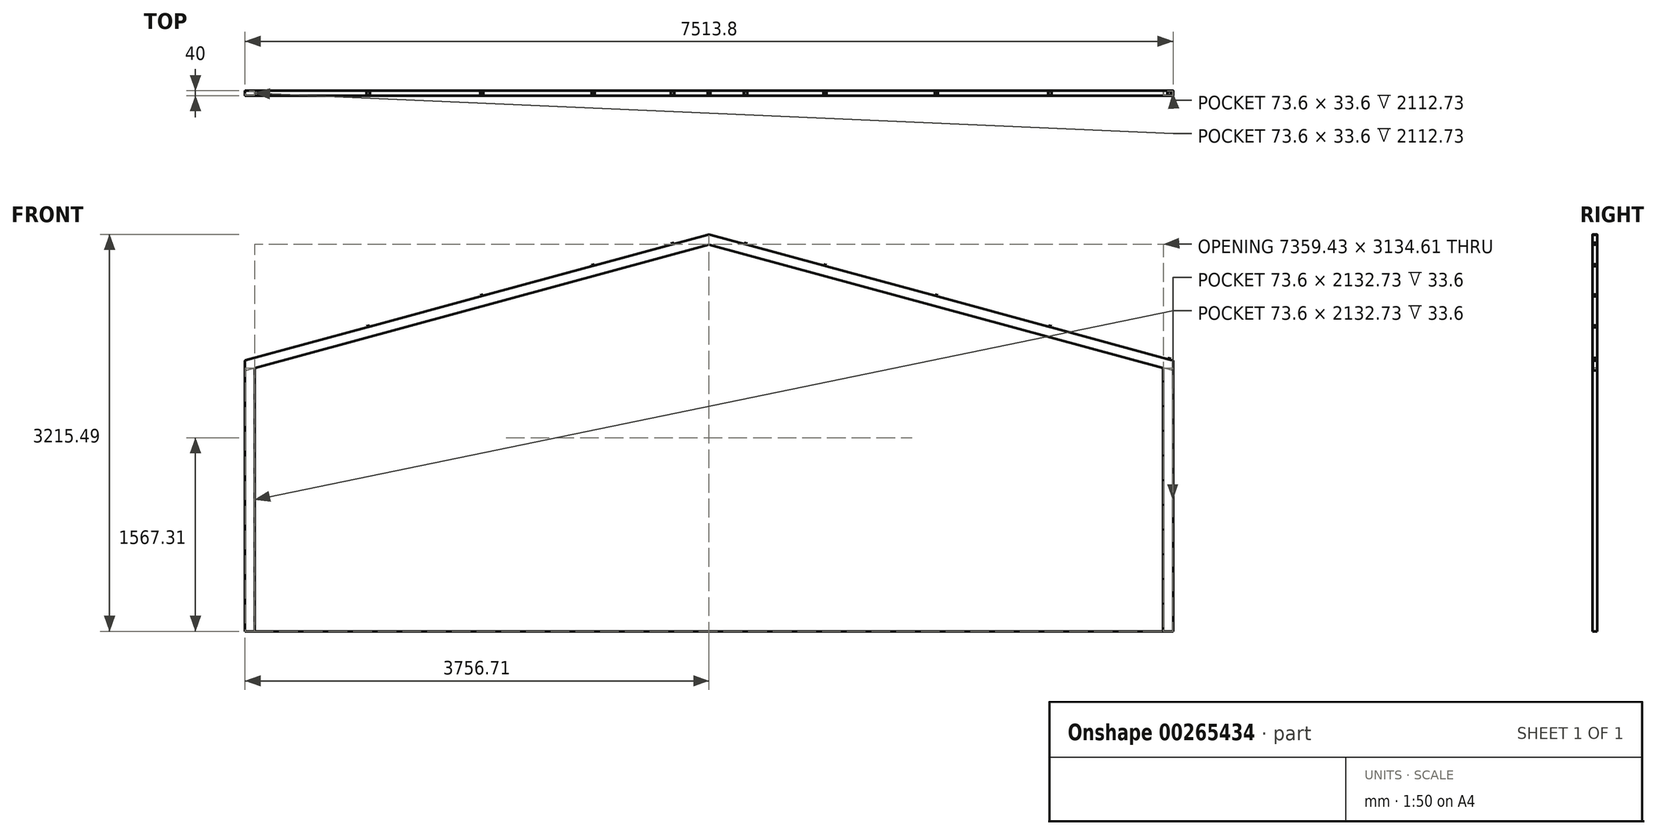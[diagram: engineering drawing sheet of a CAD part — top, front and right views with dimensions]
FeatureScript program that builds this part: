
annotation { "Feature Type Name" : "Feature", "Feature Type Description" : "" }
export const myFeature = defineFeature(function(context is Context, id is Id, definition is map)
    precondition{}
    {
        {
            var Q0;
            Q0=qCreatedBy(makeId("Top.planeOp"),FACE);
            var sketch = newSketch(context, id + "F0", { "sketchPlane" : qUnion([Q0])});
            skLineSegment(sketch, "E0.bottom", {"start": v(40, 20) * mm, "end": v(-40, 20) * mm});
            skLineSegment(sketch, "E0.top", {"start": v(40, -20) * mm, "end": v(-40, -20) * mm});
            skLineSegment(sketch, "E0.left", {"start": v(40, 20) * mm, "end": v(40, -20) * mm});
            skLineSegment(sketch, "E0.right", {"start": v(-40, 20) * mm, "end": v(-40, -20) * mm});
            skPoint(sketch, "E0.middle", {"position": v(0, 0) * mm});
            skLineSegment(sketch, "E1.bottom", {"start": v(-36.8, 16.8) * mm, "end": v(36.8, 16.8) * mm});
            skLineSegment(sketch, "E1.top", {"start": v(-36.8, -16.8) * mm, "end": v(36.8, -16.8) * mm});
            skLineSegment(sketch, "E1.left", {"start": v(-36.8, 16.8) * mm, "end": v(-36.8, -16.8) * mm});
            skLineSegment(sketch, "E1.right", {"start": v(36.8, 16.8) * mm, "end": v(36.8, -16.8) * mm});
            skSolve(sketch);
        }
        {
            var Q0;
            Q0=makeQuery(id+"F0.imprint","IMPRINT",FACE,{"disambiguationData":[TD([[makeQuery(id+"F0.imprint","IMPRINT",EDGE,{"derivedFrom":sQuery(id+"F0.wireOp",EDGE,"E0.bottom")}),1.0]])]});
            extrude(context, id + "F1", {"entities" : qUnion([Q0]), "depth" : 2133.6 * mm});
        }
        {
            var Q0;
            Q0=makeQuery(id+"F1.opExtrude","SWEPT_FACE",FACE,{"disambiguationData":[OSD([sQuery(id+"F0.wireOp",EDGE,"E0.top")])]});
            var sketch = newSketch(context, id + "F2", { "sketchPlane" : qUnion([Q0])});
            skLineSegment(sketch, "E2", {"start": v(40, 2133.6) * mm, "end": v(-40, 2111.86) * mm});
            skLineSegment(sketch, "E3", {"start": v(40, 2133.6) * mm, "end": v(19.02, 2210.8) * mm});
            skLineSegment(sketch, "E4", {"start": v(-40, 2111.86) * mm, "end": v(-60.98, 2189.07) * mm});
            skLineSegment(sketch, "E5", {"start": v(-60.98, 2189.07) * mm, "end": v(19.02, 2210.8) * mm});
            skLineSegment(sketch, "E6", {"start": v(-40, 2133.6) * mm, "end": v(-40, 2194.76) * mm});
            skSolve(sketch);
        }
        {
            var Q0;
            {var subQ0=sQuery(id+"F2.wireOp",EDGE,"E2");Q0=makeQuery(id+"F2.imprint","IMPRINT",FACE,{"disambiguationData":[TD([[makeQuery(id+"F2.imprint","IMPRINT",EDGE,{"derivedFrom":subQ0}),-1.0]])]});}
            extrude(context, id + "F3", {"entities" : qUnion([Q0]), "operationType" : NewBodyOperationType.REMOVE, "oppositeDirection" : true, "depth" : 40 * mm});
        }
        {
            var Q0;
            {var subQ0=sQuery(id+"F2.wireOp",EDGE,"E2");Q0=makeQuery(id+"F2.imprint","IMPRINT",FACE,{"disambiguationData":[TD([[makeQuery(id+"F2.imprint","IMPRINT",EDGE,{"derivedFrom":subQ0}),-1.0]])]});}
            var Q1;
            {var subQ0=sQuery(id+"F2.wireOp",EDGE,"E3");Q1=makeQuery(id+"F2.imprint","IMPRINT",FACE,{"disambiguationData":[TD([[makeQuery(id+"F2.imprint","IMPRINT",EDGE,{"derivedFrom":subQ0}),1.0]])]});}
            extrude(context, id + "F4", {"entities" : qUnion([Q0, Q1]), "operationType" : NewBodyOperationType.ADD, "oppositeDirection" : true, "depth" : 40 * mm});
        }
        {
            var Q0;
            Q0=makeQuery(id+"F4.opExtrude","SWEPT_FACE",FACE,{"disambiguationData":[OSD([sQuery(id+"F2.wireOp",EDGE,"E3")])]});
            var sketch = newSketch(context, id + "F5", { "sketchPlane" : qUnion([Q0])});
            skLineSegment(sketch, "E7.bottom", {"start": v(15.4, 2125.87) * mm, "end": v(-15.4, 2125.87) * mm});
            skLineSegment(sketch, "E7.top", {"start": v(15.4, 2051.07) * mm, "end": v(-15.4, 2051.07) * mm});
            skLineSegment(sketch, "E7.left", {"start": v(17.4, 2123.87) * mm, "end": v(17.4, 2053.07) * mm});
            skLineSegment(sketch, "E7.right", {"start": v(-17.4, 2123.87) * mm, "end": v(-17.4, 2053.07) * mm});
            skPoint(sketch, "E8.visualSharp", {"position": v(-17.4, 2125.87) * mm});
            skArc(sketch, "E8.filletArc", {"start": v(-15.4, 2125.87) * mm, "mid": v(-16.81, 2125.29) * mm, "end": v(-17.4, 2123.87) * mm});
            skPoint(sketch, "E9.visualSharp", {"position": v(17.4, 2125.87) * mm});
            skArc(sketch, "E9.filletArc", {"start": v(17.4, 2123.87) * mm, "mid": v(16.81, 2125.29) * mm, "end": v(15.4, 2125.87) * mm});
            skPoint(sketch, "E10.visualSharp", {"position": v(17.4, 2051.07) * mm});
            skArc(sketch, "E10.filletArc", {"start": v(15.4, 2051.07) * mm, "mid": v(16.81, 2051.66) * mm, "end": v(17.4, 2053.07) * mm});
            skPoint(sketch, "E11.visualSharp", {"position": v(-17.4, 2051.07) * mm});
            skArc(sketch, "E11.filletArc", {"start": v(-17.4, 2053.07) * mm, "mid": v(-16.81, 2051.66) * mm, "end": v(-15.4, 2051.07) * mm});
            skSolve(sketch);
        }
        {
            var Q0;
            Q0=makeQuery(id+"F5.imprint","IMPRINT",FACE,{"disambiguationData":[TD([[makeQuery(id+"F5.imprint","IMPRINT",EDGE,{"derivedFrom":sQuery(id+"F5.wireOp",EDGE,"E7.bottom")}),1.0]])]});
            extrude(context, id + "F6", {"entities" : qUnion([Q0]), "operationType" : NewBodyOperationType.REMOVE, "oppositeDirection" : true, "depth" : 92.3 * mm});
        }
        {
            var Q0;
            Q0=makeQuery(id+"F4.opExtrude","SWEPT_FACE",FACE,{"disambiguationData":[OSD([sQuery(id+"F2.wireOp",EDGE,"E3")])]});
            extrude(context, id + "F7", {"entities" : qUnion([Q0]), "operationType" : NewBodyOperationType.ADD, "depth" : 3810 * mm});
        }
        {
            var Q0;
            {var subQ0=sQuery(id+"F2.wireOp",EDGE,"E3");var subQ1=sQuery(id+"F0.wireOp",EDGE,"E0.top");Q0=makeQuery(id+"F7.boolean.opBoolean","MERGE",FACE,{"derivedFrom":[makeQuery(id+"F4.boolean.opBoolean","MERGE",FACE,{"derivedFrom":[makeQuery(id+"F1.opExtrude","SWEPT_FACE",FACE,{"disambiguationData":[OSD([subQ1])]}),makeQuery(id+"F4.opExtrude","CAP_FACE",FACE,{"disambiguationData":[OSD([subQ1,sQuery(id+"F0.wireOp",EDGE,"E0.right"),sQuery(id+"F2.wireOp",EDGE,"E2"),subQ0,sQuery(id+"F2.wireOp",EDGE,"E5"),sQuery(id+"F2.wireOp",EDGE,"E6")])],"isStart":true})]}),makeQuery(id+"F7.opExtrude","SWEPT_FACE",FACE,{"disambiguationData":[OSD([subQ0]),TDD([makeQuery(id+"F4.opExtrude","CAP_EDGE",EDGE,{"disambiguationData":[OSD([subQ0])],"isStart":true})])]})]});}
            var sketch = newSketch(context, id + "F8", { "sketchPlane" : qUnion([Q0])});
            skLineSegment(sketch, "E12", {"start": v(3695.74, 3209.74) * mm, "end": v(3716.71, 3215.44) * mm});
            skLineSegment(sketch, "E13", {"start": v(3716.71, 3132.54) * mm, "end": v(3716.71, 3215.44) * mm});
            skSolve(sketch);
        }
        {
            var Q0;
            Q0=makeQuery(id+"F8.imprint","IMPRINT",FACE,{"disambiguationData":[TD([[makeQuery(id+"F8.imprint","IMPRINT",EDGE,{"derivedFrom":sQuery(id+"F8.wireOp",EDGE,"E12")}),-1.0]])]});
            extrude(context, id + "F9", {"entities" : qUnion([Q0]), "operationType" : NewBodyOperationType.ADD, "oppositeDirection" : true, "depth" : 40 * mm});
        }
        {
            var Q0;
            Q0=makeQuery(id+"F9.opExtrude","SWEPT_FACE",FACE,{"disambiguationData":[OSD([sQuery(id+"F2.wireOp",EDGE,"E3")])]});
            extrude(context, id + "F10", {"entities" : qUnion([Q0]), "operationType" : NewBodyOperationType.REMOVE, "oppositeDirection" : true, "depth" : 558 * mm});
        }
        {
            var Q0;
            Q0=makeQuery(id+"F1.opExtrude","SWEPT_BODY",BODY,{"disambiguationData":[OSD([sQuery(id+"F0.wireOp",EDGE,"E0.bottom"),sQuery(id+"F0.wireOp",EDGE,"E0.top"),sQuery(id+"F0.wireOp",EDGE,"E0.left"),sQuery(id+"F0.wireOp",EDGE,"E0.right"),sQuery(id+"F0.wireOp",EDGE,"E1.bottom"),sQuery(id+"F0.wireOp",EDGE,"E1.top"),sQuery(id+"F0.wireOp",EDGE,"E1.left"),sQuery(id+"F0.wireOp",EDGE,"E1.right")])]});
            var Q1;
            Q1=makeQuery(id+"F9.opExtrude","SWEPT_FACE",FACE,{"disambiguationData":[OSD([sQuery(id+"F8.wireOp",EDGE,"E13")])]});
            mirror(context, id + "F11", {"operationType" : NewBodyOperationType.ADD, "entities" : qUnion([Q0]), "mirrorPlane" : qUnion([Q1])});
        }
        {
            var Q0;
            {var subQ0=sQuery(id+"F2.wireOp",EDGE,"E3");var subQ1=sQuery(id+"F0.wireOp",EDGE,"E0.top");var subQ2=makeQuery(id+"F9.boolean.opBoolean","MERGE",FACE,{"derivedFrom":[makeQuery(id+"F7.boolean.opBoolean","MERGE",FACE,{"derivedFrom":[makeQuery(id+"F4.boolean.opBoolean","MERGE",FACE,{"derivedFrom":[makeQuery(id+"F1.opExtrude","SWEPT_FACE",FACE,{"disambiguationData":[OSD([subQ1])]}),makeQuery(id+"F4.opExtrude","CAP_FACE",FACE,{"disambiguationData":[OSD([subQ1,sQuery(id+"F0.wireOp",EDGE,"E0.right"),sQuery(id+"F2.wireOp",EDGE,"E2"),subQ0,sQuery(id+"F2.wireOp",EDGE,"E5"),sQuery(id+"F2.wireOp",EDGE,"E6")])],"isStart":true})]}),makeQuery(id+"F7.opExtrude","SWEPT_FACE",FACE,{"disambiguationData":[OSD([subQ0]),TDD([makeQuery(id+"F4.opExtrude","CAP_EDGE",EDGE,{"disambiguationData":[OSD([subQ0])],"isStart":true})])]})]}),makeQuery(id+"F9.opExtrude","CAP_FACE",FACE,{"disambiguationData":[OSD([subQ0,sQuery(id+"F8.wireOp",EDGE,"E12"),sQuery(id+"F8.wireOp",EDGE,"E13")])],"isStart":true})]});Q0=makeQuery(id+"F11.boolean.opBoolean","MERGE",FACE,{"derivedFrom":[subQ2,makeQuery(id+"F11.opPattern","COPY",FACE,{"derivedFrom":subQ2,"instanceName":"1"})]});}
            var sketch = newSketch(context, id + "F12", { "sketchPlane" : qUnion([Q0])});
            skLineSegment(sketch, "E14", {"start": v(-6.28, 2203.93) * mm, "end": v(-18.35, 2200.65) * mm});
            skLineSegment(sketch, "E15", {"start": v(-6.28, 2203.93) * mm, "end": v(5.78, 2207.2) * mm});
            skLineSegment(sketch, "E16", {"start": v(-18.35, 2200.65) * mm, "end": v(5.78, 2207.2) * mm});
            skLineSegment(sketch, "E17", {"start": v(-18.35, 2200.65) * mm, "end": v(-20.97, 2210.3) * mm});
            skLineSegment(sketch, "E18", {"start": v(5.78, 2207.2) * mm, "end": v(3.16, 2216.85) * mm});
            skLineSegment(sketch, "E19", {"start": v(-20.97, 2210.3) * mm, "end": v(3.16, 2216.85) * mm});
            skLineSegment(sketch, "E20", {"start": v(40, 2133.6) * mm, "end": v(40, 2216.5) * mm});
            skLineSegment(sketch, "E21", {"start": v(40, 2216.5) * mm, "end": v(959.18, 2466.24) * mm});
            skLineSegment(sketch, "E22", {"start": v(959.18, 2466.24) * mm, "end": v(971.24, 2469.51) * mm});
            skLineSegment(sketch, "E23", {"start": v(959.18, 2466.24) * mm, "end": v(947.12, 2462.96) * mm});
            skLineSegment(sketch, "E24", {"start": v(947.12, 2462.96) * mm, "end": v(944.5, 2472.6) * mm});
            skLineSegment(sketch, "E25", {"start": v(971.24, 2469.51) * mm, "end": v(968.62, 2479.16) * mm});
            skLineSegment(sketch, "E26", {"start": v(944.5, 2472.6) * mm, "end": v(968.62, 2479.16) * mm});
            skLineSegment(sketch, "E27", {"start": v(40, 2216.5) * mm, "end": v(1878.36, 2715.97) * mm});
            skLineSegment(sketch, "E28", {"start": v(1878.36, 2715.97) * mm, "end": v(1890.42, 2719.25) * mm});
            skLineSegment(sketch, "E29", {"start": v(1878.36, 2715.97) * mm, "end": v(1866.3, 2712.7) * mm});
            skLineSegment(sketch, "E30", {"start": v(1866.3, 2712.7) * mm, "end": v(1863.67, 2722.34) * mm});
            skLineSegment(sketch, "E31", {"start": v(1890.42, 2719.25) * mm, "end": v(1887.8, 2728.9) * mm});
            skLineSegment(sketch, "E32", {"start": v(1863.67, 2722.34) * mm, "end": v(1887.8, 2728.9) * mm});
            skLineSegment(sketch, "E33", {"start": v(2779.68, 2960.86) * mm, "end": v(2791.74, 2964.13) * mm});
            skLineSegment(sketch, "E34", {"start": v(2779.68, 2960.86) * mm, "end": v(2767.62, 2957.58) * mm});
            skLineSegment(sketch, "E35", {"start": v(2767.62, 2957.58) * mm, "end": v(2765, 2967.23) * mm});
            skLineSegment(sketch, "E36", {"start": v(2791.74, 2964.13) * mm, "end": v(2789.12, 2973.78) * mm});
            skLineSegment(sketch, "E37", {"start": v(2767.62, 2957.58) * mm, "end": v(2779.68, 2960.86) * mm});
            skLineSegment(sketch, "E38", {"start": v(2779.68, 2960.86) * mm, "end": v(40, 2216.5) * mm});
            skLineSegment(sketch, "E39", {"start": v(2765, 2967.23) * mm, "end": v(2789.12, 2973.78) * mm});
            skLineSegment(sketch, "E40", {"start": v(3422.38, 3135.47) * mm, "end": v(3410.32, 3132.2) * mm});
            skLineSegment(sketch, "E41", {"start": v(3422.38, 3135.47) * mm, "end": v(3434.45, 3138.75) * mm});
            skLineSegment(sketch, "E42", {"start": v(3434.45, 3138.75) * mm, "end": v(3431.82, 3148.4) * mm});
            skLineSegment(sketch, "E43", {"start": v(3431.82, 3148.4) * mm, "end": v(3407.7, 3141.85) * mm});
            skLineSegment(sketch, "E44", {"start": v(3407.7, 3141.85) * mm, "end": v(3410.32, 3132.2) * mm});
            skLineSegment(sketch, "E45", {"start": v(3716.71, 3215.44) * mm, "end": v(3716.71, 3204.23) * mm});
            skLineSegment(sketch, "E46.MirrorCS", {"start": v(4011.04, 3135.47) * mm, "end": v(4023.1, 3132.2) * mm});
            skLineSegment(sketch, "E47.MirrorCS", {"start": v(4011.04, 3135.47) * mm, "end": v(3998.98, 3138.75) * mm});
            skLineSegment(sketch, "E48.MirrorCS", {"start": v(3998.98, 3138.75) * mm, "end": v(4001.6, 3148.4) * mm});
            skLineSegment(sketch, "E49.MirrorCS", {"start": v(4001.6, 3148.4) * mm, "end": v(4025.73, 3141.85) * mm});
            skLineSegment(sketch, "E50.MirrorCS", {"start": v(4025.73, 3141.85) * mm, "end": v(4023.1, 3132.2) * mm});
            skLineSegment(sketch, "E51.MirrorCS", {"start": v(4665.8, 2957.58) * mm, "end": v(4668.43, 2967.23) * mm});
            skLineSegment(sketch, "E52.MirrorCS", {"start": v(4668.43, 2967.23) * mm, "end": v(4644.3, 2973.78) * mm});
            skLineSegment(sketch, "E53.MirrorCS", {"start": v(4641.68, 2964.13) * mm, "end": v(4644.3, 2973.78) * mm});
            skLineSegment(sketch, "E54.MirrorCS", {"start": v(4653.74, 2960.86) * mm, "end": v(4641.68, 2964.13) * mm});
            skLineSegment(sketch, "E55.MirrorCS", {"start": v(5555.07, 2715.97) * mm, "end": v(5567.13, 2712.7) * mm});
            skLineSegment(sketch, "E56.MirrorCS", {"start": v(5569.75, 2722.34) * mm, "end": v(5545.63, 2728.9) * mm});
            skLineSegment(sketch, "E57.MirrorCS", {"start": v(5543, 2719.25) * mm, "end": v(5545.63, 2728.9) * mm});
            skLineSegment(sketch, "E58.MirrorCS", {"start": v(5567.13, 2712.7) * mm, "end": v(5569.75, 2722.34) * mm});
            skLineSegment(sketch, "E59.MirrorCS", {"start": v(6486.31, 2462.96) * mm, "end": v(6488.93, 2472.6) * mm});
            skLineSegment(sketch, "E60.MirrorCS", {"start": v(6488.93, 2472.6) * mm, "end": v(6464.8, 2479.16) * mm});
            skLineSegment(sketch, "E61.MirrorCS", {"start": v(6462.18, 2469.51) * mm, "end": v(6464.8, 2479.16) * mm});
            skLineSegment(sketch, "E62.MirrorCS", {"start": v(6474.25, 2466.24) * mm, "end": v(6462.18, 2469.51) * mm});
            skLineSegment(sketch, "E63.MirrorCS", {"start": v(7451.77, 2200.65) * mm, "end": v(7427.65, 2207.2) * mm});
            skLineSegment(sketch, "E64.MirrorCS", {"start": v(7451.77, 2200.65) * mm, "end": v(7454.4, 2210.3) * mm});
            skLineSegment(sketch, "E65.MirrorCS", {"start": v(7454.4, 2210.3) * mm, "end": v(7430.27, 2216.85) * mm});
            skLineSegment(sketch, "E66.MirrorCS", {"start": v(7427.65, 2207.2) * mm, "end": v(7430.27, 2216.85) * mm});
            skLineSegment(sketch, "E67", {"start": v(4653.74, 2960.86) * mm, "end": v(4665.8, 2957.58) * mm});
            skLineSegment(sketch, "E68", {"start": v(5555.07, 2715.97) * mm, "end": v(5543, 2719.25) * mm});
            skLineSegment(sketch, "E69", {"start": v(6474.25, 2466.24) * mm, "end": v(6486.31, 2462.96) * mm});
            skLineSegment(sketch, "E70", {"start": v(3716.71, 3215.44) * mm, "end": v(3422.38, 3135.47) * mm});
            skLineSegment(sketch, "E71", {"start": v(3716.71, 3215.44) * mm, "end": v(3716.71, 3215.5) * mm});
            skLineSegment(sketch, "E72", {"start": v(3716.71, 3215.44) * mm, "end": v(3704.65, 3212.16) * mm});
            skLineSegment(sketch, "E73", {"start": v(3716.71, 3215.44) * mm, "end": v(3728.78, 3212.16) * mm});
            skLineSegment(sketch, "E74", {"start": v(3704.65, 3212.16) * mm, "end": v(3704.65, 3212.21) * mm});
            skLineSegment(sketch, "E75", {"start": v(3728.78, 3212.16) * mm, "end": v(3728.78, 3212.21) * mm});
            skLineSegment(sketch, "E76", {"start": v(3728.78, 3212.21) * mm, "end": v(3716.71, 3215.5) * mm});
            skLineSegment(sketch, "E77", {"start": v(3716.71, 3215.5) * mm, "end": v(3704.65, 3212.21) * mm});
            skSolve(sketch);
        }
        {
            var Q0;
            {var subQ0=sQuery(id+"F2.wireOp",EDGE,"E5");var subQ1=sQuery(id+"F2.wireOp",EDGE,"E3");Q0=makeQuery(id+"F9.boolean.opBoolean","MERGE",EDGE,{"derivedFrom":[makeQuery(id+"F7.boolean.opBoolean","MERGE",EDGE,{"derivedFrom":[makeQuery(id+"F4.opExtrude","CAP_EDGE",EDGE,{"disambiguationData":[OSD([subQ0])],"isStart":false}),makeQuery(id+"F7.opExtrude","SWEPT_EDGE",EDGE,{"disambiguationData":[OSD([subQ1,subQ0]),TDD([makeQuery(id+"F4.opExtrude","CAP_VERTEX",VERTEX,{"disambiguationData":[OSD([subQ1,subQ0])],"isStart":false})])]})]}),makeQuery(id+"F9.opExtrude","CAP_EDGE",EDGE,{"disambiguationData":[OSD([sQuery(id+"F8.wireOp",EDGE,"E12")])],"isStart":false})]});}
            var Q1;
            {var subQ0=sQuery(id+"F2.wireOp",EDGE,"E5");var subQ1=sQuery(id+"F2.wireOp",EDGE,"E3");Q1=makeQuery(id+"F11.opPattern","COPY",EDGE,{"derivedFrom":makeQuery(id+"F9.boolean.opBoolean","MERGE",EDGE,{"derivedFrom":[makeQuery(id+"F7.boolean.opBoolean","MERGE",EDGE,{"derivedFrom":[makeQuery(id+"F4.opExtrude","CAP_EDGE",EDGE,{"disambiguationData":[OSD([subQ0])],"isStart":false}),makeQuery(id+"F7.opExtrude","SWEPT_EDGE",EDGE,{"disambiguationData":[OSD([subQ1,subQ0]),TDD([makeQuery(id+"F4.opExtrude","CAP_VERTEX",VERTEX,{"disambiguationData":[OSD([subQ1,subQ0])],"isStart":false})])]})]}),makeQuery(id+"F9.opExtrude","CAP_EDGE",EDGE,{"disambiguationData":[OSD([sQuery(id+"F8.wireOp",EDGE,"E12")])],"isStart":false})]}),"instanceName":"1"});}
            var Q2;
            {var subQ0=sQuery(id+"F2.wireOp",EDGE,"E5");var subQ1=sQuery(id+"F2.wireOp",EDGE,"E3");Q2=makeQuery(id+"F11.opPattern","COPY",EDGE,{"derivedFrom":makeQuery(id+"F9.boolean.opBoolean","MERGE",EDGE,{"derivedFrom":[makeQuery(id+"F7.boolean.opBoolean","MERGE",EDGE,{"derivedFrom":[makeQuery(id+"F4.opExtrude","CAP_EDGE",EDGE,{"disambiguationData":[OSD([subQ0])],"isStart":true}),makeQuery(id+"F7.opExtrude","SWEPT_EDGE",EDGE,{"disambiguationData":[OSD([subQ1,subQ0]),TDD([makeQuery(id+"F4.opExtrude","CAP_VERTEX",VERTEX,{"disambiguationData":[OSD([subQ1,subQ0])],"isStart":true})])]})]}),makeQuery(id+"F9.opExtrude","CAP_EDGE",EDGE,{"disambiguationData":[OSD([sQuery(id+"F8.wireOp",EDGE,"E12")])],"isStart":true})]}),"instanceName":"1"});}
            var Q3;
            {var subQ0=sQuery(id+"F2.wireOp",EDGE,"E5");var subQ1=sQuery(id+"F2.wireOp",EDGE,"E3");Q3=makeQuery(id+"F9.boolean.opBoolean","MERGE",EDGE,{"derivedFrom":[makeQuery(id+"F7.boolean.opBoolean","MERGE",EDGE,{"derivedFrom":[makeQuery(id+"F4.opExtrude","CAP_EDGE",EDGE,{"disambiguationData":[OSD([subQ0])],"isStart":true}),makeQuery(id+"F7.opExtrude","SWEPT_EDGE",EDGE,{"disambiguationData":[OSD([subQ1,subQ0]),TDD([makeQuery(id+"F4.opExtrude","CAP_VERTEX",VERTEX,{"disambiguationData":[OSD([subQ1,subQ0])],"isStart":true})])]})]}),makeQuery(id+"F9.opExtrude","CAP_EDGE",EDGE,{"disambiguationData":[OSD([sQuery(id+"F8.wireOp",EDGE,"E12")])],"isStart":true})]});}
            var Q4;
            Q4=makeQuery(id+"F11.opPattern","COPY",EDGE,{"derivedFrom":makeQuery(id+"F7.opExtrude","SWEPT_EDGE",EDGE,{"disambiguationData":[OSD([sQuery(id+"F0.wireOp",EDGE,"E0.bottom"),sQuery(id+"F0.wireOp",EDGE,"E0.top"),sQuery(id+"F0.wireOp",EDGE,"E0.left"),sQuery(id+"F2.wireOp",EDGE,"E2"),sQuery(id+"F2.wireOp",EDGE,"E3")])]}),"instanceName":"1"});
            var Q5;
            Q5=makeQuery(id+"F7.opExtrude","SWEPT_EDGE",EDGE,{"disambiguationData":[OSD([sQuery(id+"F0.wireOp",EDGE,"E0.bottom"),sQuery(id+"F0.wireOp",EDGE,"E0.top"),sQuery(id+"F0.wireOp",EDGE,"E0.left"),sQuery(id+"F2.wireOp",EDGE,"E2"),sQuery(id+"F2.wireOp",EDGE,"E3")])]});
            var Q6;
            Q6=makeQuery(id+"F7.opExtrude","SWEPT_EDGE",EDGE,{"disambiguationData":[OSD([sQuery(id+"F0.wireOp",EDGE,"E0.top"),sQuery(id+"F0.wireOp",EDGE,"E0.left"),sQuery(id+"F2.wireOp",EDGE,"E2"),sQuery(id+"F2.wireOp",EDGE,"E3")])]});
            var Q7;
            Q7=makeQuery(id+"F11.opPattern","COPY",EDGE,{"derivedFrom":makeQuery(id+"F7.opExtrude","SWEPT_EDGE",EDGE,{"disambiguationData":[OSD([sQuery(id+"F0.wireOp",EDGE,"E0.top"),sQuery(id+"F0.wireOp",EDGE,"E0.left"),sQuery(id+"F2.wireOp",EDGE,"E2"),sQuery(id+"F2.wireOp",EDGE,"E3")])]}),"instanceName":"1"});
            fillet(context, id + "F13", {"entities" : qUnion([Q0, Q1, Q2, Q3, Q4, Q5, Q6, Q7]), "radius" : 2 * mm, "tangentPropagation" : true, "allowEdgeOverflow" : false});
        }
        {
            var Q0;
            Q0=makeQuery(id+"F1.opExtrude","SWEPT_EDGE",EDGE,{"disambiguationData":[OSD([sQuery(id+"F0.wireOp",EDGE,"E0.top"),sQuery(id+"F0.wireOp",EDGE,"E0.left")])]});
            var Q1;
            Q1=makeQuery(id+"F1.opExtrude","SWEPT_EDGE",EDGE,{"disambiguationData":[OSD([sQuery(id+"F0.wireOp",EDGE,"E0.bottom"),sQuery(id+"F0.wireOp",EDGE,"E0.left")])]});
            var Q2;
            {var subQ0=sQuery(id+"F0.wireOp",EDGE,"E0.right");Q2=makeQuery(id+"F4.boolean.opBoolean","MERGE",EDGE,{"derivedFrom":[makeQuery(id+"F1.opExtrude","SWEPT_EDGE",EDGE,{"disambiguationData":[OSD([sQuery(id+"F0.wireOp",EDGE,"E0.bottom"),subQ0])]}),makeQuery(id+"F4.opExtrude","CAP_EDGE",EDGE,{"disambiguationData":[OSD([sQuery(id+"F0.wireOp",EDGE,"E0.top"),subQ0,sQuery(id+"F2.wireOp",EDGE,"E6")])],"isStart":false})]});}
            var Q3;
            {var subQ0=sQuery(id+"F0.wireOp",EDGE,"E0.right");var subQ1=sQuery(id+"F0.wireOp",EDGE,"E0.top");Q3=makeQuery(id+"F11.opPattern","COPY",EDGE,{"derivedFrom":makeQuery(id+"F4.boolean.opBoolean","MERGE",EDGE,{"derivedFrom":[makeQuery(id+"F1.opExtrude","SWEPT_EDGE",EDGE,{"disambiguationData":[OSD([subQ1,subQ0])]}),makeQuery(id+"F4.opExtrude","CAP_EDGE",EDGE,{"disambiguationData":[OSD([subQ1,subQ0,sQuery(id+"F2.wireOp",EDGE,"E6")])],"isStart":true})]}),"instanceName":"1"});}
            var Q4;
            {var subQ0=sQuery(id+"F0.wireOp",EDGE,"E0.right");Q4=makeQuery(id+"F11.opPattern","COPY",EDGE,{"derivedFrom":makeQuery(id+"F4.boolean.opBoolean","MERGE",EDGE,{"derivedFrom":[makeQuery(id+"F1.opExtrude","SWEPT_EDGE",EDGE,{"disambiguationData":[OSD([sQuery(id+"F0.wireOp",EDGE,"E0.bottom"),subQ0])]}),makeQuery(id+"F4.opExtrude","CAP_EDGE",EDGE,{"disambiguationData":[OSD([sQuery(id+"F0.wireOp",EDGE,"E0.top"),subQ0,sQuery(id+"F2.wireOp",EDGE,"E6")])],"isStart":false})]}),"instanceName":"1"});}
            var Q5;
            Q5=makeQuery(id+"F11.opPattern","COPY",EDGE,{"derivedFrom":makeQuery(id+"F1.opExtrude","SWEPT_EDGE",EDGE,{"disambiguationData":[OSD([sQuery(id+"F0.wireOp",EDGE,"E0.bottom"),sQuery(id+"F0.wireOp",EDGE,"E0.left")])]}),"instanceName":"1"});
            var Q6;
            Q6=makeQuery(id+"F11.opPattern","COPY",EDGE,{"derivedFrom":makeQuery(id+"F1.opExtrude","SWEPT_EDGE",EDGE,{"disambiguationData":[OSD([sQuery(id+"F0.wireOp",EDGE,"E0.top"),sQuery(id+"F0.wireOp",EDGE,"E0.left")])]}),"instanceName":"1"});
            fillet(context, id + "F14", {"entities" : qUnion([Q0, Q1, Q2, Q3, Q4, Q5, Q6]), "radius" : 3 * mm, "tangentPropagation" : true, "allowEdgeOverflow" : false});
        }
        {
            var Q0;
            {var subQ0=sQuery(id+"F0.wireOp",EDGE,"E0.right");Q0=makeQuery(id+"F14.opFillet","SPLIT",FACE,{"disambiguationData":[OD(1.0)],"derivedFrom":makeQuery(id+"F4.boolean.opBoolean","MERGE",FACE,{"derivedFrom":[makeQuery(id+"F1.opExtrude","SWEPT_FACE",FACE,{"disambiguationData":[OSD([subQ0])]}),makeQuery(id+"F4.opExtrude","SWEPT_FACE",FACE,{"disambiguationData":[OSD([sQuery(id+"F0.wireOp",EDGE,"E0.top"),subQ0,sQuery(id+"F2.wireOp",EDGE,"E6")])]})]})});}
            var sketch = newSketch(context, id + "F15", { "sketchPlane" : qUnion([Q0])});
            skLineSegment(sketch, "E78", {"start": v(0, 0) * mm, "end": v(-20, 0) * mm});
            skLineSegment(sketch, "E79.bottom", {"start": v(-20, 0) * mm, "end": v(20, 0) * mm});
            skLineSegment(sketch, "E79.top", {"start": v(-20, 0) * mm, "end": v(20, 0) * mm});
            skLineSegment(sketch, "E79.left", {"start": v(-20, 0) * mm, "end": v(-20, 0) * mm});
            skLineSegment(sketch, "E79.right", {"start": v(20, 0) * mm, "end": v(20, 0) * mm});
            skSolve(sketch);
        }
        {
            var Q0;
            Q0=makeQuery(id+"F15.imprint","IMPRINT",FACE,{"disambiguationData":[TD([[makeQuery(id+"F15.imprint","IMPRINT",EDGE,{"derivedFrom":sQuery(id+"F15.wireOp",EDGE,"E79.top")}),1.0]])]});
            extrude(context, id + "F16", {"entities" : qUnion([Q0]), "operationType" : NewBodyOperationType.ADD, "oppositeDirection" : true, "depth" : 7513.8 * mm});
        }
        {
            var Q0;
            Q0=makeQuery(id+"F12.imprint","IMPRINT",FACE,{"disambiguationData":[TD([[makeQuery(id+"F12.imprint","IMPRINT",EDGE,{"derivedFrom":sQuery(id+"F12.wireOp",EDGE,"E16")}),1.0]])]});
            var Q1;
            {var subQ1=sQuery(id+"F12.wireOp",EDGE,"E24");Q1=makeQuery(id+"F12.imprint","IMPRINT",FACE,{"disambiguationData":[TD([[makeQuery(id+"F12.imprint","IMPRINT",EDGE,{"derivedFrom":subQ1}),-1.0]])]});}
            var Q2;
            {var subQ1=sQuery(id+"F12.wireOp",EDGE,"E30");Q2=makeQuery(id+"F12.imprint","IMPRINT",FACE,{"disambiguationData":[TD([[makeQuery(id+"F12.imprint","IMPRINT",EDGE,{"derivedFrom":subQ1}),-1.0]])]});}
            var Q3;
            {var subQ1=sQuery(id+"F12.wireOp",EDGE,"E35");Q3=makeQuery(id+"F12.imprint","IMPRINT",FACE,{"disambiguationData":[TD([[makeQuery(id+"F12.imprint","IMPRINT",EDGE,{"derivedFrom":subQ1}),-1.0]])]});}
            var Q4;
            Q4=makeQuery(id+"F12.imprint","IMPRINT",FACE,{"disambiguationData":[TD([[makeQuery(id+"F12.imprint","IMPRINT",EDGE,{"derivedFrom":sQuery(id+"F12.wireOp",EDGE,"E40")}),1.0]])]});
            var Q5;
            {var subQ7=sQuery(id+"F12.wireOp",EDGE,"rvYJcqt1-21Oj-p3wZ-czKF-GlUjLanXVYOE");Q5=makeQuery(id+"F12.imprint","IMPRINT",FACE,{"disambiguationData":[TD([[makeQuery(id+"F12.imprint","IMPRINT",EDGE,{"derivedFrom":subQ7}),-1.0]])]});}
            var Q6;
            Q6=makeQuery(id+"F12.imprint","IMPRINT",FACE,{"disambiguationData":[TD([[makeQuery(id+"F12.imprint","IMPRINT",EDGE,{"derivedFrom":sQuery(id+"F12.wireOp",EDGE,"E46.MirrorCS")}),-1.0]])]});
            var Q7;
            Q7=makeQuery(id+"F12.imprint","IMPRINT",FACE,{"disambiguationData":[TD([[makeQuery(id+"F12.imprint","IMPRINT",EDGE,{"derivedFrom":sQuery(id+"F12.wireOp",EDGE,"E51.MirrorCS")}),1.0]])]});
            var Q8;
            Q8=makeQuery(id+"F12.imprint","IMPRINT",FACE,{"disambiguationData":[TD([[makeQuery(id+"F12.imprint","IMPRINT",EDGE,{"derivedFrom":sQuery(id+"F12.wireOp",EDGE,"E55.MirrorCS")}),-1.0]])]});
            var Q9;
            Q9=makeQuery(id+"F12.imprint","IMPRINT",FACE,{"disambiguationData":[TD([[makeQuery(id+"F12.imprint","IMPRINT",EDGE,{"derivedFrom":sQuery(id+"F12.wireOp",EDGE,"E59.MirrorCS")}),1.0]])]});
            var Q10;
            Q10=makeQuery(id+"F12.imprint","IMPRINT",FACE,{"disambiguationData":[TD([[makeQuery(id+"F12.imprint","IMPRINT",EDGE,{"derivedFrom":sQuery(id+"F12.wireOp",EDGE,"E63.MirrorCS")}),-1.0]])]});
            extrude(context, id + "F17", {"entities" : qUnion([Q0, Q1, Q2, Q3, Q4, Q5, Q6, Q7, Q8, Q9, Q10]), "operationType" : NewBodyOperationType.ADD, "oppositeDirection" : true, "depth" : 40 * mm});
        }
        {
            var Q0;
            Q0=makeQuery(id+"F12.imprint","IMPRINT",FACE,{"disambiguationData":[TD([[makeQuery(id+"F12.imprint","IMPRINT",EDGE,{"derivedFrom":sQuery(id+"F12.wireOp",EDGE,"E16")}),1.0]])]});
            var Q1;
            {var subQ1=sQuery(id+"F12.wireOp",EDGE,"E24");Q1=makeQuery(id+"F12.imprint","IMPRINT",FACE,{"disambiguationData":[TD([[makeQuery(id+"F12.imprint","IMPRINT",EDGE,{"derivedFrom":subQ1}),-1.0]])]});}
            var Q2;
            {var subQ1=sQuery(id+"F12.wireOp",EDGE,"E30");Q2=makeQuery(id+"F12.imprint","IMPRINT",FACE,{"disambiguationData":[TD([[makeQuery(id+"F12.imprint","IMPRINT",EDGE,{"derivedFrom":subQ1}),-1.0]])]});}
            var Q3;
            {var subQ1=sQuery(id+"F12.wireOp",EDGE,"E33");Q3=makeQuery(id+"F12.imprint","IMPRINT",FACE,{"disambiguationData":[TD([[makeQuery(id+"F12.imprint","IMPRINT",EDGE,{"derivedFrom":subQ1}),1.0]])]});}
            var Q4;
            {var subQ1=sQuery(id+"F12.wireOp",EDGE,"E40");Q4=makeQuery(id+"F12.imprint","IMPRINT",FACE,{"disambiguationData":[TD([[makeQuery(id+"F12.imprint","IMPRINT",EDGE,{"derivedFrom":subQ1}),1.0]])]});}
            var Q5;
            Q5=makeQuery(id+"F12.imprint","IMPRINT",FACE,{"disambiguationData":[TD([[makeQuery(id+"F12.imprint","IMPRINT",EDGE,{"derivedFrom":sQuery(id+"F12.wireOp",EDGE,"E71")}),1.0]])]});
            var Q6;
            Q6=makeQuery(id+"F12.imprint","IMPRINT",FACE,{"disambiguationData":[TD([[makeQuery(id+"F12.imprint","IMPRINT",EDGE,{"derivedFrom":sQuery(id+"F12.wireOp",EDGE,"E71")}),-1.0]])]});
            var Q7;
            Q7=makeQuery(id+"F12.imprint","IMPRINT",FACE,{"disambiguationData":[TD([[makeQuery(id+"F12.imprint","IMPRINT",EDGE,{"derivedFrom":sQuery(id+"F12.wireOp",EDGE,"E46.MirrorCS")}),-1.0]])]});
            var Q8;
            Q8=makeQuery(id+"F12.imprint","IMPRINT",FACE,{"disambiguationData":[TD([[makeQuery(id+"F12.imprint","IMPRINT",EDGE,{"derivedFrom":sQuery(id+"F12.wireOp",EDGE,"E51.MirrorCS")}),1.0]])]});
            var Q9;
            Q9=makeQuery(id+"F12.imprint","IMPRINT",FACE,{"disambiguationData":[TD([[makeQuery(id+"F12.imprint","IMPRINT",EDGE,{"derivedFrom":sQuery(id+"F12.wireOp",EDGE,"E55.MirrorCS")}),-1.0]])]});
            var Q10;
            Q10=makeQuery(id+"F12.imprint","IMPRINT",FACE,{"disambiguationData":[TD([[makeQuery(id+"F12.imprint","IMPRINT",EDGE,{"derivedFrom":sQuery(id+"F12.wireOp",EDGE,"E59.MirrorCS")}),1.0]])]});
            var Q11;
            Q11=makeQuery(id+"F12.imprint","IMPRINT",FACE,{"disambiguationData":[TD([[makeQuery(id+"F12.imprint","IMPRINT",EDGE,{"derivedFrom":sQuery(id+"F12.wireOp",EDGE,"E63.MirrorCS")}),-1.0]])]});
            extrude(context, id + "F18", {"entities" : qUnion([Q0, Q1, Q2, Q3, Q4, Q5, Q6, Q7, Q8, Q9, Q10, Q11]), "operationType" : NewBodyOperationType.ADD, "oppositeDirection" : true, "depth" : 40 * mm});
        }
        {
            var Q0;
            Q0=makeQuery(id+"F18.opExtrude","CAP_FACE",FACE,{"disambiguationData":[OSD([sQuery(id+"F12.wireOp",EDGE,"E72"),sQuery(id+"F12.wireOp",EDGE,"E73"),sQuery(id+"F12.wireOp",EDGE,"E74"),sQuery(id+"F12.wireOp",EDGE,"E75"),sQuery(id+"F12.wireOp",EDGE,"E76"),sQuery(id+"F12.wireOp",EDGE,"E77")])],"isStart":false});
            var Q1;
            Q1=makeQuery(id+"F17.opExtrude","CAP_FACE",FACE,{"disambiguationData":[OSD([sQuery(id+"F12.wireOp",EDGE,"E40"),sQuery(id+"F12.wireOp",EDGE,"E42"),sQuery(id+"F12.wireOp",EDGE,"E43"),sQuery(id+"F12.wireOp",EDGE,"E44"),sQuery(id+"F12.wireOp",EDGE,"E70")])],"isStart":false});
            var Q2;
            Q2=makeQuery(id+"F17.opExtrude","CAP_FACE",FACE,{"disambiguationData":[OSD([sQuery(id+"F12.wireOp",EDGE,"E33"),sQuery(id+"F12.wireOp",EDGE,"E35"),sQuery(id+"F12.wireOp",EDGE,"E36"),sQuery(id+"F12.wireOp",EDGE,"E38"),sQuery(id+"F12.wireOp",EDGE,"E39")])],"isStart":false});
            var Q3;
            Q3=makeQuery(id+"F17.opExtrude","CAP_FACE",FACE,{"disambiguationData":[OSD([sQuery(id+"F12.wireOp",EDGE,"E30"),sQuery(id+"F12.wireOp",EDGE,"E31"),sQuery(id+"F12.wireOp",EDGE,"E32"),sQuery(id+"F12.wireOp",EDGE,"E38")])],"isStart":false});
            var Q4;
            Q4=makeQuery(id+"F17.opExtrude","CAP_FACE",FACE,{"disambiguationData":[OSD([sQuery(id+"F12.wireOp",EDGE,"E24"),sQuery(id+"F12.wireOp",EDGE,"E25"),sQuery(id+"F12.wireOp",EDGE,"E26"),sQuery(id+"F12.wireOp",EDGE,"E38")])],"isStart":false});
            var Q5;
            Q5=makeQuery(id+"F17.opExtrude","CAP_FACE",FACE,{"disambiguationData":[OSD([sQuery(id+"F12.wireOp",EDGE,"E16"),sQuery(id+"F12.wireOp",EDGE,"E17"),sQuery(id+"F12.wireOp",EDGE,"E18"),sQuery(id+"F12.wireOp",EDGE,"E19")])],"isStart":false});
            var Q6;
            Q6=makeQuery(id+"F17.opExtrude","CAP_FACE",FACE,{"disambiguationData":[OSD([sQuery(id+"F12.wireOp",EDGE,"E46.MirrorCS"),sQuery(id+"F12.wireOp",EDGE,"E47.MirrorCS"),sQuery(id+"F12.wireOp",EDGE,"E48.MirrorCS"),sQuery(id+"F12.wireOp",EDGE,"E49.MirrorCS"),sQuery(id+"F12.wireOp",EDGE,"E50.MirrorCS")])],"isStart":false});
            var Q7;
            Q7=makeQuery(id+"F17.opExtrude","CAP_FACE",FACE,{"disambiguationData":[OSD([sQuery(id+"F12.wireOp",EDGE,"E51.MirrorCS"),sQuery(id+"F12.wireOp",EDGE,"E52.MirrorCS"),sQuery(id+"F12.wireOp",EDGE,"E53.MirrorCS"),sQuery(id+"F12.wireOp",EDGE,"E54.MirrorCS"),sQuery(id+"F12.wireOp",EDGE,"E67")])],"isStart":false});
            var Q8;
            Q8=makeQuery(id+"F17.opExtrude","CAP_FACE",FACE,{"disambiguationData":[OSD([sQuery(id+"F12.wireOp",EDGE,"E55.MirrorCS"),sQuery(id+"F12.wireOp",EDGE,"E56.MirrorCS"),sQuery(id+"F12.wireOp",EDGE,"E57.MirrorCS"),sQuery(id+"F12.wireOp",EDGE,"E58.MirrorCS"),sQuery(id+"F12.wireOp",EDGE,"E68")])],"isStart":false});
            var Q9;
            Q9=makeQuery(id+"F17.opExtrude","CAP_FACE",FACE,{"disambiguationData":[OSD([sQuery(id+"F12.wireOp",EDGE,"E59.MirrorCS"),sQuery(id+"F12.wireOp",EDGE,"E60.MirrorCS"),sQuery(id+"F12.wireOp",EDGE,"E61.MirrorCS"),sQuery(id+"F12.wireOp",EDGE,"E62.MirrorCS"),sQuery(id+"F12.wireOp",EDGE,"E69")])],"isStart":false});
            var Q10;
            Q10=makeQuery(id+"F17.opExtrude","CAP_FACE",FACE,{"disambiguationData":[OSD([sQuery(id+"F12.wireOp",EDGE,"E63.MirrorCS"),sQuery(id+"F12.wireOp",EDGE,"E64.MirrorCS"),sQuery(id+"F12.wireOp",EDGE,"E65.MirrorCS"),sQuery(id+"F12.wireOp",EDGE,"E66.MirrorCS")])],"isStart":false});
            extrude(context, id + "F19", {"entities" : qUnion([Q0, Q1, Q2, Q3, Q4, Q5, Q6, Q7, Q8, Q9, Q10]), "operationType" : NewBodyOperationType.REMOVE, "oppositeDirection" : true, "depth" : 2 * mm});
        }
        {
            var Q0;
            Q0=makeQuery(id+"F18.opExtrude","CAP_FACE",FACE,{"disambiguationData":[OSD([sQuery(id+"F12.wireOp",EDGE,"E72"),sQuery(id+"F12.wireOp",EDGE,"E73"),sQuery(id+"F12.wireOp",EDGE,"E74"),sQuery(id+"F12.wireOp",EDGE,"E75"),sQuery(id+"F12.wireOp",EDGE,"E76"),sQuery(id+"F12.wireOp",EDGE,"E77")])],"isStart":true});
            var Q1;
            Q1=makeQuery(id+"F17.opExtrude","CAP_FACE",FACE,{"disambiguationData":[OSD([sQuery(id+"F12.wireOp",EDGE,"E16"),sQuery(id+"F12.wireOp",EDGE,"E17"),sQuery(id+"F12.wireOp",EDGE,"E18"),sQuery(id+"F12.wireOp",EDGE,"E19")])],"isStart":true});
            var Q2;
            Q2=makeQuery(id+"F17.opExtrude","CAP_FACE",FACE,{"disambiguationData":[OSD([sQuery(id+"F12.wireOp",EDGE,"E24"),sQuery(id+"F12.wireOp",EDGE,"E25"),sQuery(id+"F12.wireOp",EDGE,"E26"),sQuery(id+"F12.wireOp",EDGE,"E38")])],"isStart":true});
            var Q3;
            Q3=makeQuery(id+"F17.opExtrude","CAP_FACE",FACE,{"disambiguationData":[OSD([sQuery(id+"F12.wireOp",EDGE,"E30"),sQuery(id+"F12.wireOp",EDGE,"E31"),sQuery(id+"F12.wireOp",EDGE,"E32"),sQuery(id+"F12.wireOp",EDGE,"E38")])],"isStart":true});
            var Q4;
            Q4=makeQuery(id+"F17.opExtrude","CAP_FACE",FACE,{"disambiguationData":[OSD([sQuery(id+"F12.wireOp",EDGE,"E33"),sQuery(id+"F12.wireOp",EDGE,"E35"),sQuery(id+"F12.wireOp",EDGE,"E36"),sQuery(id+"F12.wireOp",EDGE,"E38"),sQuery(id+"F12.wireOp",EDGE,"E39")])],"isStart":true});
            var Q5;
            Q5=makeQuery(id+"F17.opExtrude","CAP_FACE",FACE,{"disambiguationData":[OSD([sQuery(id+"F12.wireOp",EDGE,"E40"),sQuery(id+"F12.wireOp",EDGE,"E42"),sQuery(id+"F12.wireOp",EDGE,"E43"),sQuery(id+"F12.wireOp",EDGE,"E44"),sQuery(id+"F12.wireOp",EDGE,"E70")])],"isStart":true});
            var Q6;
            Q6=makeQuery(id+"F17.opExtrude","CAP_FACE",FACE,{"disambiguationData":[OSD([sQuery(id+"F12.wireOp",EDGE,"E46.MirrorCS"),sQuery(id+"F12.wireOp",EDGE,"E47.MirrorCS"),sQuery(id+"F12.wireOp",EDGE,"E48.MirrorCS"),sQuery(id+"F12.wireOp",EDGE,"E49.MirrorCS"),sQuery(id+"F12.wireOp",EDGE,"E50.MirrorCS")])],"isStart":true});
            var Q7;
            Q7=makeQuery(id+"F17.opExtrude","CAP_FACE",FACE,{"disambiguationData":[OSD([sQuery(id+"F12.wireOp",EDGE,"E51.MirrorCS"),sQuery(id+"F12.wireOp",EDGE,"E52.MirrorCS"),sQuery(id+"F12.wireOp",EDGE,"E53.MirrorCS"),sQuery(id+"F12.wireOp",EDGE,"E54.MirrorCS"),sQuery(id+"F12.wireOp",EDGE,"E67")])],"isStart":true});
            var Q8;
            Q8=makeQuery(id+"F17.opExtrude","CAP_FACE",FACE,{"disambiguationData":[OSD([sQuery(id+"F12.wireOp",EDGE,"E55.MirrorCS"),sQuery(id+"F12.wireOp",EDGE,"E56.MirrorCS"),sQuery(id+"F12.wireOp",EDGE,"E57.MirrorCS"),sQuery(id+"F12.wireOp",EDGE,"E58.MirrorCS"),sQuery(id+"F12.wireOp",EDGE,"E68")])],"isStart":true});
            var Q9;
            Q9=makeQuery(id+"F17.opExtrude","CAP_FACE",FACE,{"disambiguationData":[OSD([sQuery(id+"F12.wireOp",EDGE,"E59.MirrorCS"),sQuery(id+"F12.wireOp",EDGE,"E60.MirrorCS"),sQuery(id+"F12.wireOp",EDGE,"E61.MirrorCS"),sQuery(id+"F12.wireOp",EDGE,"E62.MirrorCS"),sQuery(id+"F12.wireOp",EDGE,"E69")])],"isStart":true});
            var Q10;
            Q10=makeQuery(id+"F17.opExtrude","CAP_FACE",FACE,{"disambiguationData":[OSD([sQuery(id+"F12.wireOp",EDGE,"E63.MirrorCS"),sQuery(id+"F12.wireOp",EDGE,"E64.MirrorCS"),sQuery(id+"F12.wireOp",EDGE,"E65.MirrorCS"),sQuery(id+"F12.wireOp",EDGE,"E66.MirrorCS")])],"isStart":true});
            extrude(context, id + "F20", {"entities" : qUnion([Q0, Q1, Q2, Q3, Q4, Q5, Q6, Q7, Q8, Q9, Q10]), "operationType" : NewBodyOperationType.REMOVE, "oppositeDirection" : true, "depth" : 2 * mm});
        }
    });
